# Revit family: GMA
name_source: partatom
category: Air Terminals
revit_build: Autodesk Revit MEP 2012 (Build: 20110309_2315(x64)
units: mm (PartAtom-declared; Revit-internal decimal feet)

## types (4) — shared parameters
Alto rejilla = 3/4"
Ancho barra = 1/16"
Ancho rejilla = 5/32"
Largo barra = 1/4"
Manufacturer = INNES
Máxima presión estática = 0.00 in-wg
Máxima velocidad de cuello = 0 FPM
Mínima presión estática = 0.00 in-wg
Mínima velocidad de cuello = 0 FPM
Separacion = 7/32"
Separacion barras = 1"
URL = http://www.innes.com.mx

## per-type parameters (varying)
| type | A Largo | A barras | A parilla | B | Height | Largo parilla | No. de elementos | No. de elementos barras | Width |
| GMA-12-08 | 11 3/4" | 10 7/32" | 10 21/32" | 7 3/4" | 9 3/4" | 6 7/8" | 31 | 10 | 13 3/4" |
| GMA-13-09 | 12 3/4" | 11 7/32" | 11 21/32" | 8 3/4" | 10 3/4" | 7 7/8" | 36 | 11 | 14 3/4" |
| GMA-14-10 | 13 3/4" | 12 7/32" | 12 21/32" | 9 3/4" | 11 3/4" | 8 7/8" | 41 | 12 | 15 3/4" |
| GMA-15-11 | 14 3/4" | 13 7/32" | 13 21/32" | 10 3/4" | 12 3/4" | 9 7/8" | 45 | 13 | 16 3/4" |

## geometry (parser evidence)
native form markers: Blend x3, Sweep x5
no freeform markers — native parametric forms only
